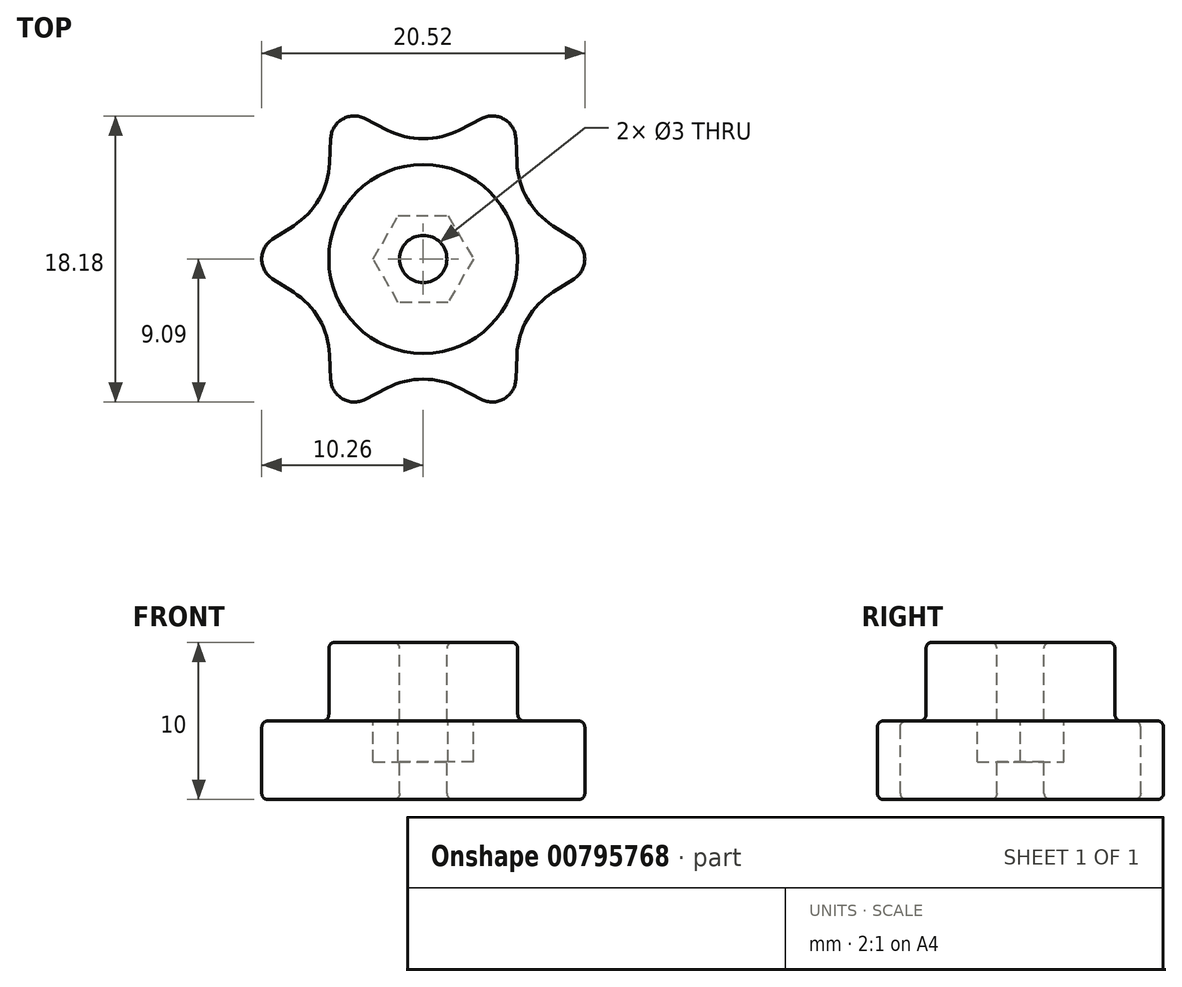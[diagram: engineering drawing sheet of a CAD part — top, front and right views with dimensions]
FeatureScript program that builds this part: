
annotation { "Feature Type Name" : "Feature", "Feature Type Description" : "" }
export const myFeature = defineFeature(function(context is Context, id is Id, definition is map)
    precondition{}
    {
        {
            var Q0;
            Q0=qCreatedBy(makeId("Top.planeOp"),FACE);
            var sketch = newSketch(context, id + "F0", { "sketchPlane" : qUnion([Q0])});
            skCircle(sketch, "E0", {"center": v(0, 0) * mm, "radius": 6 * mm});
            skCircle(sketch, "E1", {"center": v(0, 0) * mm, "radius": 1.5 * mm});
            skCircle(sketch, "E2.0", {"center": v(0, 0) * mm, "radius": 7 * mm, "construction": true});
            skCircle(sketch, "E3.cCircle", {"center": v(0, 0) * mm, "radius": 10 * mm, "construction": true});
            skLineSegment(sketch, "E3.0", {"start": v(-5.77, 10) * mm, "end": v(5.77, 10) * mm, "construction": true});
            skLineSegment(sketch, "E3.1", {"start": v(5.77, 10) * mm, "end": v(11.55, 0) * mm, "construction": true});
            skLineSegment(sketch, "E3.2", {"start": v(11.55, 0) * mm, "end": v(5.77, -10) * mm, "construction": true});
            skLineSegment(sketch, "E3.3", {"start": v(5.77, -10) * mm, "end": v(-5.77, -10) * mm, "construction": true});
            skLineSegment(sketch, "E3.4", {"start": v(-5.77, -10) * mm, "end": v(-11.55, 0) * mm, "construction": true});
            skLineSegment(sketch, "E3.5", {"start": v(-11.55, 0) * mm, "end": v(-5.77, 10) * mm, "construction": true});
            skPoint(sketch, "E3.0.midPoint", {"position": v(0, 10) * mm});
            skLineSegment(sketch, "E4", {"start": v(0, 10) * mm, "end": v(0, 7) * mm, "construction": true});
            skLineSegment(sketch, "E5", {"start": v(5.77, 10) * mm, "end": v(0, 7) * mm});
            skLineSegment(sketch, "E6", {"start": v(-5.77, 10) * mm, "end": v(0, 7) * mm});
            skLineSegment(sketch, "E7.1.0", {"start": v(-5.77, 10) * mm, "end": v(-6.06, 3.5) * mm});
            skLineSegment(sketch, "E7.1.1", {"start": v(-11.55, 0) * mm, "end": v(-6.06, 3.5) * mm});
            skLineSegment(sketch, "E7.2.0", {"start": v(-11.55, 0) * mm, "end": v(-6.06, -3.5) * mm});
            skLineSegment(sketch, "E7.2.1", {"start": v(-5.77, -10) * mm, "end": v(-6.06, -3.5) * mm});
            skLineSegment(sketch, "E7.3.0", {"start": v(-5.77, -10) * mm, "end": v(0, -7) * mm});
            skLineSegment(sketch, "E7.3.1", {"start": v(5.77, -10) * mm, "end": v(0, -7) * mm});
            skLineSegment(sketch, "E7.4.0", {"start": v(5.77, -10) * mm, "end": v(6.06, -3.5) * mm});
            skLineSegment(sketch, "E7.4.1", {"start": v(11.55, 0) * mm, "end": v(6.06, -3.5) * mm});
            skLineSegment(sketch, "E7.5.0", {"start": v(11.55, 0) * mm, "end": v(6.06, 3.5) * mm});
            skLineSegment(sketch, "E7.5.1", {"start": v(5.77, 10) * mm, "end": v(6.06, 3.5) * mm});
            skCircle(sketch, "E8.cCircle", {"center": v(0, 0) * mm, "radius": 2.75 * mm, "construction": true});
            skLineSegment(sketch, "E8.0", {"start": v(-1.59, 2.75) * mm, "end": v(1.59, 2.75) * mm});
            skLineSegment(sketch, "E8.1", {"start": v(1.59, 2.75) * mm, "end": v(3.18, 0) * mm});
            skLineSegment(sketch, "E8.2", {"start": v(3.18, 0) * mm, "end": v(1.59, -2.75) * mm});
            skLineSegment(sketch, "E8.3", {"start": v(1.59, -2.75) * mm, "end": v(-1.59, -2.75) * mm});
            skLineSegment(sketch, "E8.4", {"start": v(-1.59, -2.75) * mm, "end": v(-3.18, 0) * mm});
            skLineSegment(sketch, "E8.5", {"start": v(-3.18, 0) * mm, "end": v(-1.59, 2.75) * mm});
            skPoint(sketch, "E8.0.midPoint", {"position": v(0, 2.75) * mm});
            skSolve(sketch);
        }
        {
            var Q0;
            Q0=makeQuery(id+"F0.imprint","IMPRINT",FACE,{"disambiguationData":[TD([[makeQuery(id+"F0.imprint","IMPRINT",EDGE,{"derivedFrom":sQuery(id+"F0.wireOp",EDGE,"E0")}),-1.0]])]});
            var Q1;
            Q1=makeQuery(id+"F0.imprint","IMPRINT",FACE,{"disambiguationData":[TD([[makeQuery(id+"F0.imprint","IMPRINT",EDGE,{"derivedFrom":sQuery(id+"F0.wireOp",EDGE,"E0")}),1.0]])]});
            var Q2;
            Q2=makeQuery(id+"F0.imprint","IMPRINT",FACE,{"disambiguationData":[TD([[makeQuery(id+"F0.imprint","IMPRINT",EDGE,{"derivedFrom":sQuery(id+"F0.wireOp",EDGE,"E1")}),-1.0]])]});
            extrude(context, id + "F1", {"entities" : qUnion([Q0, Q1, Q2]), "oppositeDirection" : true, "depth" : 5 * mm, "offsetDistance" : 25 * mm});
        }
        {
            var Q0;
            Q0=makeQuery(id+"F0.imprint","IMPRINT",FACE,{"disambiguationData":[TD([[makeQuery(id+"F0.imprint","IMPRINT",EDGE,{"derivedFrom":sQuery(id+"F0.wireOp",EDGE,"E0")}),1.0]])]});
            var Q1;
            Q1=makeQuery(id+"F0.imprint","IMPRINT",FACE,{"disambiguationData":[TD([[makeQuery(id+"F0.imprint","IMPRINT",EDGE,{"derivedFrom":sQuery(id+"F0.wireOp",EDGE,"E1")}),-1.0]])]});
            extrude(context, id + "F2", {"entities" : qUnion([Q0, Q1]), "operationType" : NewBodyOperationType.ADD, "depth" : 5 * mm, "offsetDistance" : 25 * mm});
        }
        {
            var Q0;
            Q0=makeQuery(id+"F0.imprint","IMPRINT",FACE,{"disambiguationData":[TD([[makeQuery(id+"F0.imprint","IMPRINT",EDGE,{"derivedFrom":sQuery(id+"F0.wireOp",EDGE,"E1")}),-1.0]])]});
            extrude(context, id + "F3", {"entities" : qUnion([Q0]), "operationType" : NewBodyOperationType.REMOVE, "oppositeDirection" : true, "depth" : 2.6 * mm, "offsetDistance" : 25 * mm});
        }
        {
            var Q0;
            Q0=makeQuery(id+"F1.opExtrude","SWEPT_EDGE",EDGE,{"disambiguationData":[OSD([sQuery(id+"F0.wireOp",EDGE,"E7.1.1"),sQuery(id+"F0.wireOp",EDGE,"E7.2.0")])]});
            var Q1;
            Q1=makeQuery(id+"F1.opExtrude","SWEPT_EDGE",EDGE,{"disambiguationData":[OSD([sQuery(id+"F0.wireOp",EDGE,"E7.2.1"),sQuery(id+"F0.wireOp",EDGE,"E7.3.0")])]});
            var Q2;
            Q2=makeQuery(id+"F1.opExtrude","SWEPT_EDGE",EDGE,{"disambiguationData":[OSD([sQuery(id+"F0.wireOp",EDGE,"E7.3.1"),sQuery(id+"F0.wireOp",EDGE,"E7.4.0")])]});
            var Q3;
            Q3=makeQuery(id+"F1.opExtrude","SWEPT_EDGE",EDGE,{"disambiguationData":[OSD([sQuery(id+"F0.wireOp",EDGE,"E7.4.1"),sQuery(id+"F0.wireOp",EDGE,"E7.5.0")])]});
            var Q4;
            Q4=makeQuery(id+"F1.opExtrude","SWEPT_EDGE",EDGE,{"disambiguationData":[OSD([sQuery(id+"F0.wireOp",EDGE,"E5"),sQuery(id+"F0.wireOp",EDGE,"E7.5.1")])]});
            var Q5;
            Q5=makeQuery(id+"F1.opExtrude","SWEPT_EDGE",EDGE,{"disambiguationData":[OSD([sQuery(id+"F0.wireOp",EDGE,"E6"),sQuery(id+"F0.wireOp",EDGE,"E7.1.0")])]});
            fillet(context, id + "F4", {"entities" : qUnion([Q0, Q1, Q2, Q3, Q4, Q5]), "radius" : 1.5 * mm, "tangentPropagation" : true, "allowEdgeOverflow" : false});
        }
        {
            var Q0;
            Q0=makeQuery(id+"F1.opExtrude","SWEPT_EDGE",EDGE,{"disambiguationData":[OSD([sQuery(id+"F0.wireOp",EDGE,"E7.4.0"),sQuery(id+"F0.wireOp",EDGE,"E7.4.1")])]});
            var Q1;
            Q1=makeQuery(id+"F1.opExtrude","SWEPT_EDGE",EDGE,{"disambiguationData":[OSD([sQuery(id+"F0.wireOp",EDGE,"E7.5.0"),sQuery(id+"F0.wireOp",EDGE,"E7.5.1")])]});
            var Q2;
            Q2=makeQuery(id+"F1.opExtrude","SWEPT_EDGE",EDGE,{"disambiguationData":[OSD([sQuery(id+"F0.wireOp",EDGE,"E5"),sQuery(id+"F0.wireOp",EDGE,"E6")])]});
            var Q3;
            Q3=makeQuery(id+"F1.opExtrude","SWEPT_EDGE",EDGE,{"disambiguationData":[OSD([sQuery(id+"F0.wireOp",EDGE,"E7.1.0"),sQuery(id+"F0.wireOp",EDGE,"E7.1.1")])]});
            var Q4;
            Q4=makeQuery(id+"F1.opExtrude","SWEPT_EDGE",EDGE,{"disambiguationData":[OSD([sQuery(id+"F0.wireOp",EDGE,"E7.2.0"),sQuery(id+"F0.wireOp",EDGE,"E7.2.1")])]});
            var Q5;
            Q5=makeQuery(id+"F1.opExtrude","SWEPT_EDGE",EDGE,{"disambiguationData":[OSD([sQuery(id+"F0.wireOp",EDGE,"E7.3.0"),sQuery(id+"F0.wireOp",EDGE,"E7.3.1")])]});
            fillet(context, id + "F5", {"entities" : qUnion([Q0, Q1, Q2, Q3, Q4, Q5]), "radius" : 5 * mm, "tangentPropagation" : true, "allowEdgeOverflow" : false});
        }
        {
            var Q0;
            Q0=makeQuery(id+"F1.opExtrude","CAP_FACE",FACE,{"disambiguationData":[OSD([sQuery(id+"F0.wireOp",EDGE,"E1"),sQuery(id+"F0.wireOp",EDGE,"E5"),sQuery(id+"F0.wireOp",EDGE,"E6"),sQuery(id+"F0.wireOp",EDGE,"E7.1.0"),sQuery(id+"F0.wireOp",EDGE,"E7.1.1"),sQuery(id+"F0.wireOp",EDGE,"E7.2.0"),sQuery(id+"F0.wireOp",EDGE,"E7.2.1"),sQuery(id+"F0.wireOp",EDGE,"E7.3.0"),sQuery(id+"F0.wireOp",EDGE,"E7.3.1"),sQuery(id+"F0.wireOp",EDGE,"E7.4.0"),sQuery(id+"F0.wireOp",EDGE,"E7.4.1"),sQuery(id+"F0.wireOp",EDGE,"E7.5.0"),sQuery(id+"F0.wireOp",EDGE,"E7.5.1")])],"isStart":true});
            var Q1;
            Q1=makeQuery(id+"F1.opExtrude","CAP_FACE",FACE,{"disambiguationData":[OSD([sQuery(id+"F0.wireOp",EDGE,"E1"),sQuery(id+"F0.wireOp",EDGE,"E5"),sQuery(id+"F0.wireOp",EDGE,"E6"),sQuery(id+"F0.wireOp",EDGE,"E7.1.0"),sQuery(id+"F0.wireOp",EDGE,"E7.1.1"),sQuery(id+"F0.wireOp",EDGE,"E7.2.0"),sQuery(id+"F0.wireOp",EDGE,"E7.2.1"),sQuery(id+"F0.wireOp",EDGE,"E7.3.0"),sQuery(id+"F0.wireOp",EDGE,"E7.3.1"),sQuery(id+"F0.wireOp",EDGE,"E7.4.0"),sQuery(id+"F0.wireOp",EDGE,"E7.4.1"),sQuery(id+"F0.wireOp",EDGE,"E7.5.0"),sQuery(id+"F0.wireOp",EDGE,"E7.5.1")])],"isStart":false});
            var Q2;
            Q2=makeQuery(id+"F2.opExtrude","CAP_FACE",FACE,{"disambiguationData":[OSD([sQuery(id+"F0.wireOp",EDGE,"E0"),sQuery(id+"F0.wireOp",EDGE,"E1")])],"isStart":false});
            fillet(context, id + "F6", {"entities" : qUnion([Q0, Q1, Q2]), "radius" : 0.4 * mm, "tangentPropagation" : true, "allowEdgeOverflow" : false});
        }
    });
